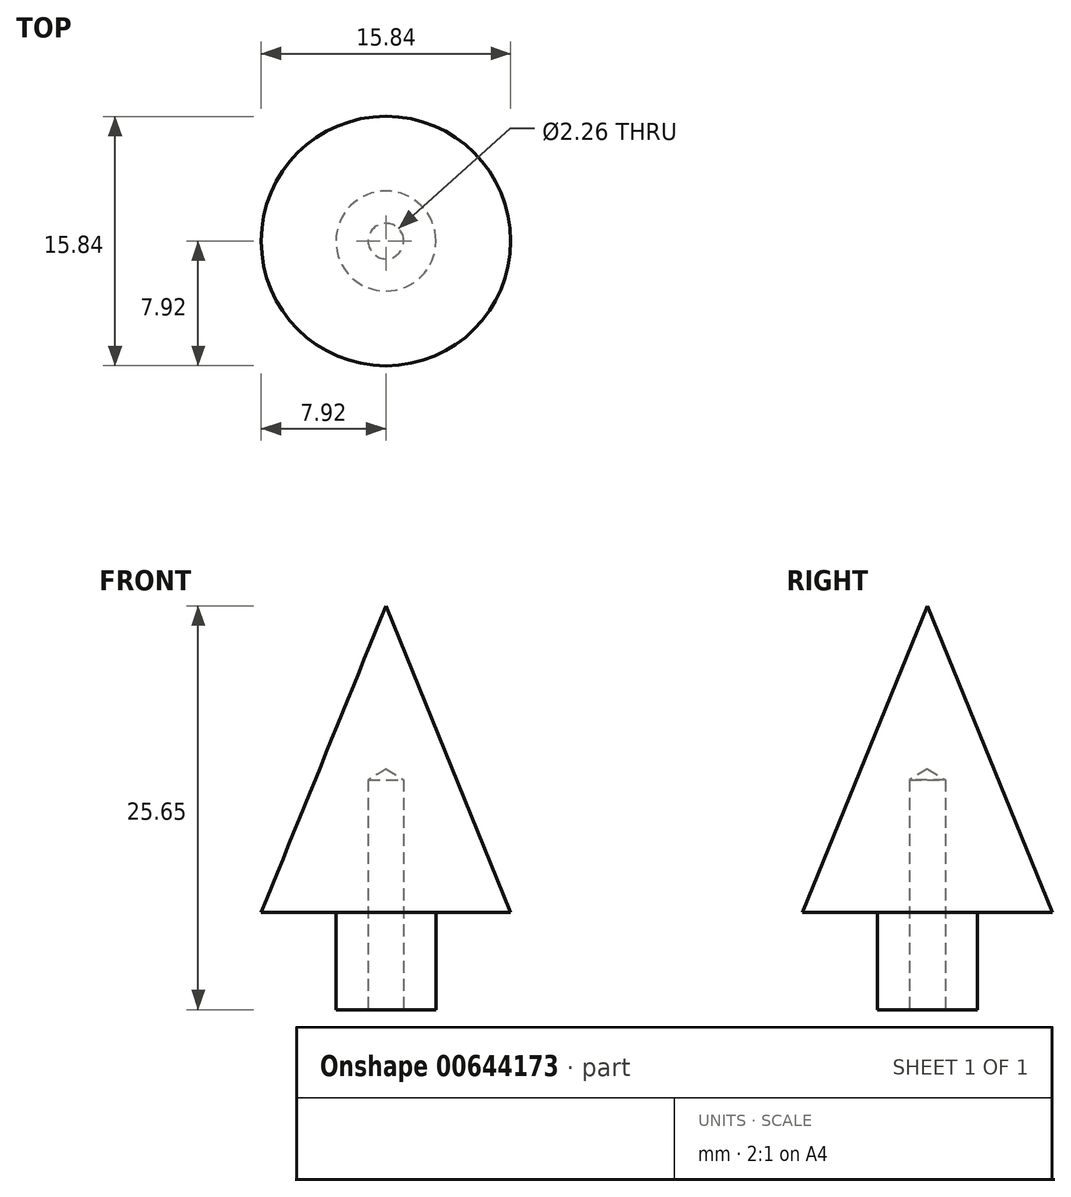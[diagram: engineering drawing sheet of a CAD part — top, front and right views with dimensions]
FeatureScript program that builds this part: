
annotation { "Feature Type Name" : "Feature", "Feature Type Description" : "" }
export const myFeature = defineFeature(function(context is Context, id is Id, definition is map)
    precondition{}
    {
        {
            var Q0;
            Q0=qCreatedBy(makeId("Front.planeOp"),FACE);
            var sketch = newSketch(context, id + "F0", { "sketchPlane" : qUnion([Q0])});
            skLineSegment(sketch, "E0", {"start": v(0, 19.48) * mm, "end": v(-7.92, 0) * mm});
            skLineSegment(sketch, "E1", {"start": v(-7.92, 0) * mm, "end": v(-3.18, 0) * mm});
            skLineSegment(sketch, "E2", {"start": v(-3.18, 0) * mm, "end": v(-3.18, -6.17) * mm});
            skLineSegment(sketch, "E3", {"start": v(-3.18, -6.17) * mm, "end": v(0, -6.17) * mm});
            skLineSegment(sketch, "E4", {"start": v(0, -6.17) * mm, "end": v(0, 0) * mm});
            skLineSegment(sketch, "E5", {"start": v(0, 0) * mm, "end": v(0, 19.48) * mm});
            skSolve(sketch);
        }
        {
            var Q0;
            Q0=makeQuery(id+"F0.imprint","IMPRINT",FACE,{"disambiguationData":[TD([[makeQuery(id+"F0.imprint","IMPRINT",EDGE,{"derivedFrom":sQuery(id+"F0.wireOp",EDGE,"E0")}),1.0]])]});
            var Q1;
            Q1=sQuery(id+"F0.wireOp",EDGE,"E5");
            revolve(context, id + "F1", {"entities" : qUnion([Q0]), "axis" : qUnion([Q1]), "revolveType" : RevolveType.FULL});
        }
        {
            var Q0;
            Q0=makeQuery(id+"F1.opRevolve","SWEPT_FACE",FACE,{"disambiguationData":[OSD([sQuery(id+"F0.wireOp",EDGE,"E3")])]});
            var sketch = newSketch(context, id + "F2", { "sketchPlane" : qUnion([Q0])});
            skPoint(sketch, "E6", {"position": v(0, 0) * mm});
            skSolve(sketch);
        }
        {
            var Q0;
            Q0=sQuery(id+"F2.wireOp",VERTEX,"E6");
            var Q1;
            Q1=makeQuery(id+"F1.opRevolve","SWEPT_BODY",BODY,{"disambiguationData":[OSD([sQuery(id+"F0.wireOp",EDGE,"E0"),sQuery(id+"F0.wireOp",EDGE,"E1"),sQuery(id+"F0.wireOp",EDGE,"E2"),sQuery(id+"F0.wireOp",EDGE,"E3"),sQuery(id+"F0.wireOp",EDGE,"E4"),sQuery(id+"F0.wireOp",EDGE,"E5")])]});
            hole(context, id + "F3", {"style" : HoleStyle.SIMPLE, "endStyle" : HoleEndStyle.BLIND, "standardTappedOrClearance" : lookupTablePath({ "standard" : "ANSI", "engagement" : "75%", "pitch" : "40 tpi", "size" : "#4", "type" : "Tapped" }), "standardBlindInLast" : lookupTablePath({ "standard" : "ANSI", "engagement" : "75%", "pitch" : "40 tpi", "size" : "#4", "type" : "Tapped" }), "holeDiameter" : 2.26 * mm, "majorDiameter" : 2.84 * mm, "showTappedDepth" : true, "holeDepth" : 14.6 * mm, "isTappedThrough" : true, "tappedDepth" : 12.7 * mm, "tapClearance" : 3, "locations" : qUnion([Q0]), "scope" : qUnion([Q1])});
        }
    });
